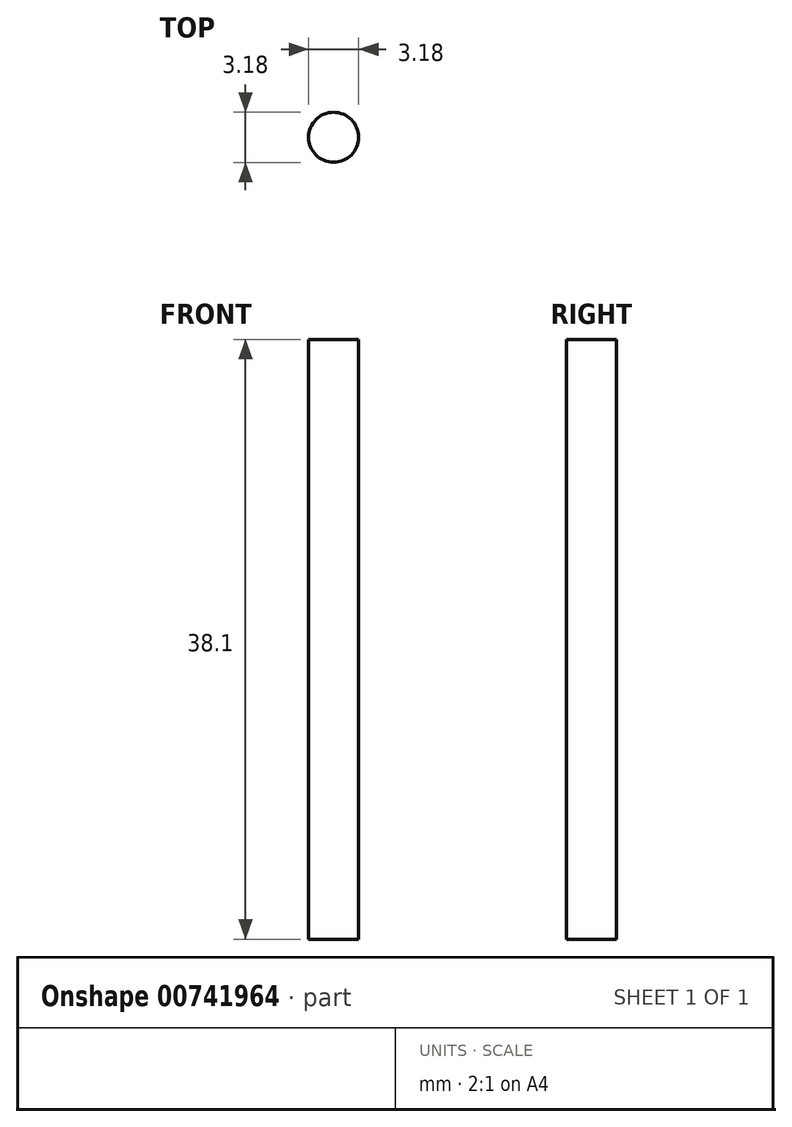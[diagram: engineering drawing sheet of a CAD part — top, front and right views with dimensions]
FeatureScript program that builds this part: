
annotation { "Feature Type Name" : "Feature", "Feature Type Description" : "" }
export const myFeature = defineFeature(function(context is Context, id is Id, definition is map)
    precondition{}
    {
        {
            var Q0;
            Q0=qCreatedBy(makeId("Top.planeOp"),FACE);
            var sketch = newSketch(context, id + "F0", { "sketchPlane" : qUnion([Q0])});
            skCircle(sketch, "E0", {"center": v(0, 0) * mm, "radius": 1.59 * mm});
            skSolve(sketch);
        }
        {
            var Q0;
            Q0 = qSketchRegion(id + "F0", true);
            extrude(context, id + "F1", {"entities" : qUnion([Q0]), "depth" : 38.1 * mm, "offsetDistance" : 25.4 * mm});
        }
    });
